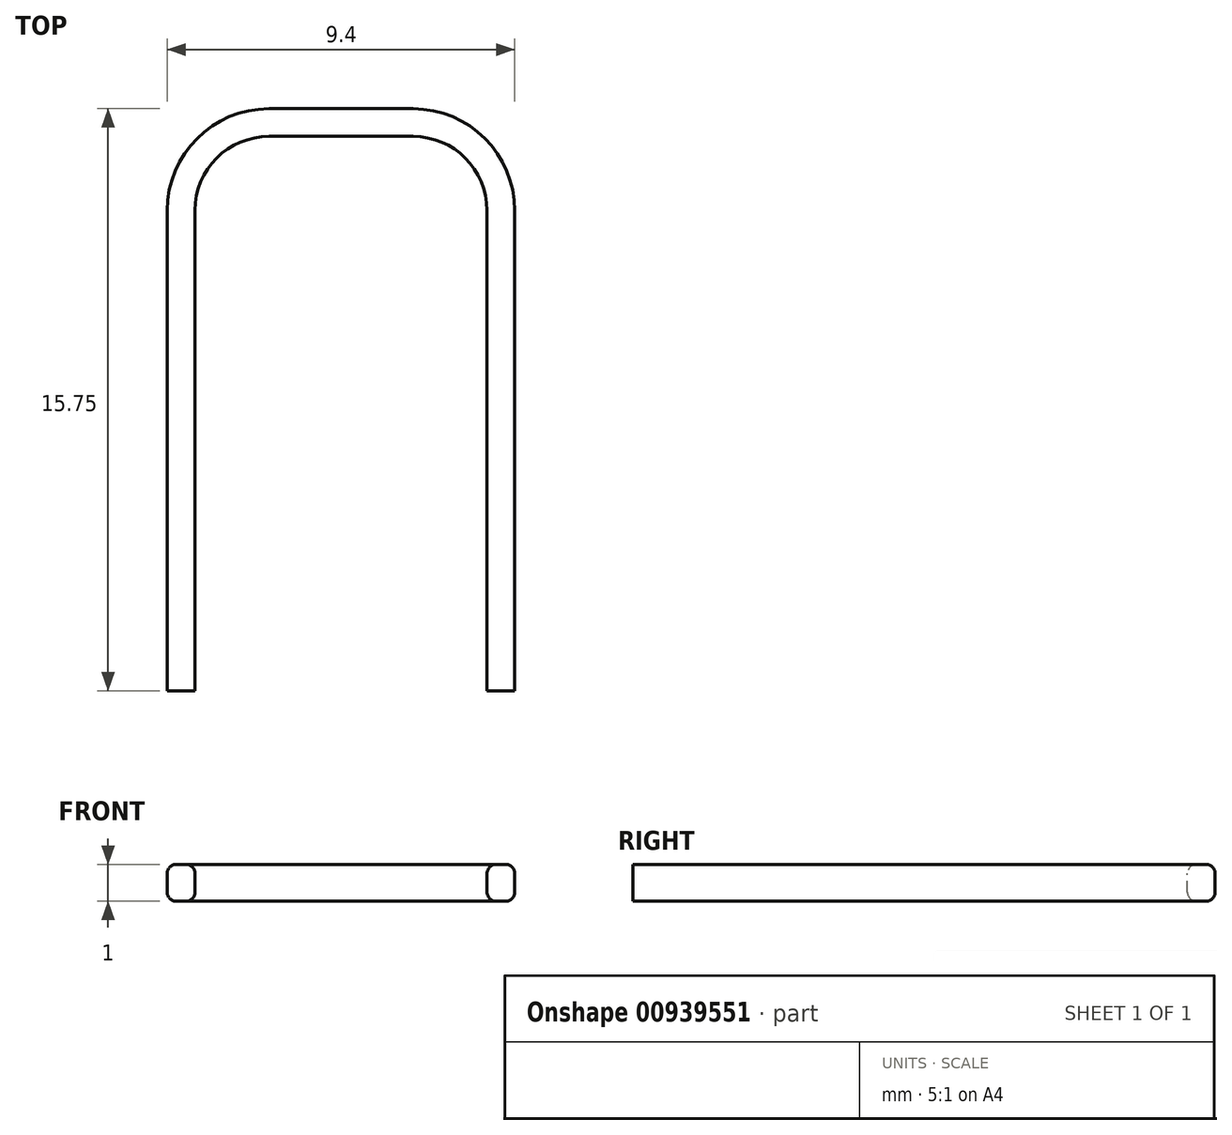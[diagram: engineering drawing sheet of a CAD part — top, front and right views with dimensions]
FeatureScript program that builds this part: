
annotation { "Feature Type Name" : "Feature", "Feature Type Description" : "" }
export const myFeature = defineFeature(function(context is Context, id is Id, definition is map)
    precondition{}
    {
        {
            var Q0;
            Q0=qCreatedBy(makeId("Top.planeOp"),FACE);
            var sketch = newSketch(context, id + "F0", { "sketchPlane" : qUnion([Q0])});
            skLineSegment(sketch, "E0", {"start": v(-3.95, 0) * mm, "end": v(-3.95, 13) * mm});
            skLineSegment(sketch, "E1", {"start": v(-1.95, 15) * mm, "end": v(1.95, 15) * mm});
            skLineSegment(sketch, "E2", {"start": v(3.95, 13) * mm, "end": v(3.95, 0) * mm});
            skPoint(sketch, "E3.visualSharp", {"position": v(-3.95, 15) * mm});
            skArc(sketch, "E3.filletArc", {"start": v(-1.95, 15) * mm, "mid": v(-3.36, 14.41) * mm, "end": v(-3.95, 13) * mm});
            skPoint(sketch, "E4.visualSharp", {"position": v(3.95, 15) * mm});
            skArc(sketch, "E4.filletArc", {"start": v(3.95, 13) * mm, "mid": v(3.36, 14.41) * mm, "end": v(1.95, 15) * mm});
            skSolve(sketch);
        }
        {
            var Q0;
            Q0=qCreatedBy(makeId("Front.planeOp"),FACE);
            var sketch = newSketch(context, id + "F1", { "sketchPlane" : qUnion([Q0])});
            skLineSegment(sketch, "E5.bottom", {"start": v(-3.95, 0) * mm, "end": v(-4.7, 0) * mm});
            skLineSegment(sketch, "E5.top", {"start": v(-3.95, 1) * mm, "end": v(-4.7, 1) * mm});
            skLineSegment(sketch, "E5.left", {"start": v(-3.95, 0) * mm, "end": v(-3.95, 1) * mm});
            skLineSegment(sketch, "E5.right", {"start": v(-4.7, 0) * mm, "end": v(-4.7, 1) * mm});
            skSolve(sketch);
        }
        {
            var Q0;
            Q0 = qSketchRegion(id + "F1", true);
            var Q1;
            Q1 = qConstructionFilter(qBodyType(qCreatedBy(id + "F0" ,EDGE), BodyType.WIRE), ConstructionObject.NO);
            sweep(context, id + "F2", {"profiles" : qUnion([Q0]), "path" : qUnion([Q1])});
        }
        {
            var Q0;
            Q0=makeQuery(id+"F2.opSweep","SWEPT_EDGE",EDGE,{"disambiguationData":[OSD([sQuery(id+"F0.wireOp",EDGE,"E0"),sQuery(id+"F1.wireOp",EDGE,"E5.top"),sQuery(id+"F1.wireOp",EDGE,"E5.right")])]});
            var Q1;
            Q1=makeQuery(id+"F2.opSweep","SWEPT_EDGE",EDGE,{"disambiguationData":[OSD([sQuery(id+"F0.wireOp",EDGE,"E0"),sQuery(id+"F1.wireOp",EDGE,"E5.top"),sQuery(id+"F1.wireOp",EDGE,"E5.left")])]});
            var Q2;
            Q2=makeQuery(id+"F2.opSweep","SWEPT_EDGE",EDGE,{"disambiguationData":[OSD([sQuery(id+"F0.wireOp",EDGE,"E2"),sQuery(id+"F1.wireOp",EDGE,"E5.bottom"),sQuery(id+"F1.wireOp",EDGE,"E5.left")])]});
            var Q3;
            Q3=makeQuery(id+"F2.opSweep","SWEPT_EDGE",EDGE,{"disambiguationData":[OSD([sQuery(id+"F0.wireOp",EDGE,"E2"),sQuery(id+"F1.wireOp",EDGE,"E5.bottom"),sQuery(id+"F1.wireOp",EDGE,"E5.right")])]});
            fillet(context, id + "F3", {"entities" : qUnion([Q0, Q1, Q2, Q3]), "radius" : .25 * mm, "tangentPropagation" : true, "allowEdgeOverflow" : false});
        }
    });
